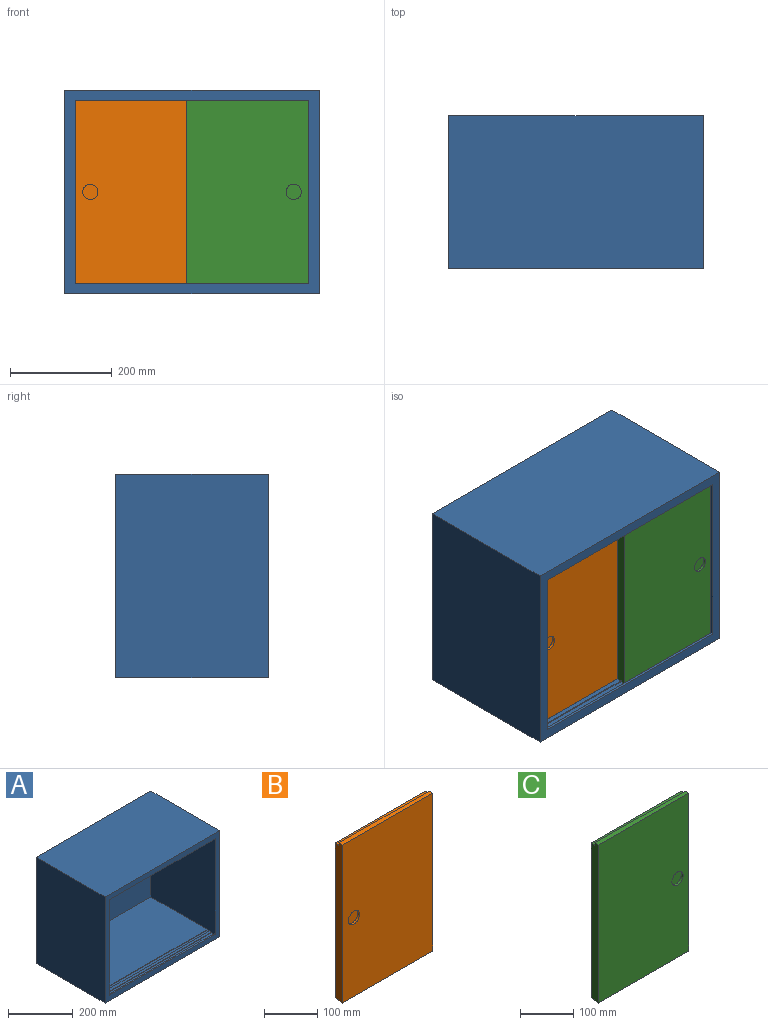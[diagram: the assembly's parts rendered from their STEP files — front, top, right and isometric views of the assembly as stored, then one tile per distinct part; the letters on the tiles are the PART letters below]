
ASSEMBLY  parts=3 mates=2
PART A: 27 faces, bbox 500x300x400 mm
  f0: plane 460x10mm, normal (0,0,-1), area 4600mm2, adj f10,f12,f21,f24
  f1: plane 460x245mm, normal (0,0,-1), area 112700mm2, adj f10,f11,f12,f22
  f2: plane 460x10mm, normal (0,0,1), area 4600mm2, adj f10,f12,f17,f19
  f3: plane 460x245mm, normal (0,0,1), area 112700mm2, adj f10,f11,f12,f16
  f4: plane 500x400mm, normal (0,-1,0), area 34400mm2, adj f5,f7,f8,f9,f10,f12,f13,f14
  f5: plane 400x300mm, normal (1,0,0), area 120000mm2, adj f4,f6,f8,f9
  f6: plane 500x400mm, normal (0,1,0), area 200000mm2, adj f5,f7,f8,f9
  f7: plane 400x300mm, normal (-1,0,0), area 120000mm2, adj f4,f6,f8,f9
  f8: plane 500x300mm, normal (0,0,1), area 150000mm2, adj f4,f5,f6,f7
  f9: plane 500x300mm, normal (0,0,-1), area 150000mm2, adj f4,f5,f6,f7
  f10: plane 367x280mm, normal (-1,0,0), area 100940mm2, adj f0,f1,f2,f3,f4,f11,f13,f14
  f11: plane 460x360mm, normal (0,-1,0), area 165600mm2, adj f1,f3,f10,f12
  f12: plane 367x280mm, normal (1,0,0), area 100940mm2, adj f0,f1,f2,f3,f4,f11,f13,f14
  f13: plane 460x5mm, normal (0,0,-1), area 2300mm2, adj f4,f10,f12,f25
  f14: plane 460x5mm, normal (0,0,1), area 2300mm2, adj f4,f10,f12,f20
  f15: plane 460x10mm, normal (0,0,1), area 4600mm2, adj f10,f12,f16,f17
  f16: plane 460x2mm, normal (0,-1,0), area 920mm2, adj f3,f10,f12,f15
  f17: plane 460x2mm, normal (0,1,0), area 920mm2, adj f2,f10,f12,f15
  f18: plane 460x10mm, normal (0,0,1), area 4600mm2, adj f10,f12,f19,f20
  f19: plane 460x2mm, normal (0,-1,0), area 920mm2, adj f2,f10,f12,f18
  f20: plane 460x2mm, normal (0,1,0), area 920mm2, adj f10,f12,f14,f18
  f21: plane 460x5mm, normal (0,1,0), area 2300mm2, adj f0,f10,f12,f23
  f22: plane 460x5mm, normal (0,-1,0), area 2300mm2, adj f1,f10,f12,f23
  f23: plane 460x10mm, normal (0,0,-1), area 4600mm2, adj f10,f12,f21,f22
  f24: plane 460x5mm, normal (0,-1,0), area 2300mm2, adj f0,f10,f12,f26
  f25: plane 460x5mm, normal (0,1,0), area 2300mm2, adj f10,f12,f13,f26
  f26: plane 460x10mm, normal (0,0,-1), area 4600mm2, adj f10,f12,f24,f25
PART B: 12 faces, bbox 240x20x364.5 mm
  f0: plane 240x5mm, normal (0,1,0), area 1200mm2, adj f2,f3,f8,f9
  f1: plane 364.5x240mm, normal (0,-1,0), area 86773.1mm2, adj f2,f3,f5,f8,f10
  f2: plane 364.5x20mm, normal (1,0,0), area 7220mm2, adj f0,f1,f4,f5,f6,f7,f8,f9
  f3: plane 364.5x20mm, normal (-1,0,0), area 7220mm2, adj f0,f1,f4,f5,f6,f7,f8,f9
  f4: plane 357.5x240mm, normal (0,1,0), area 85800mm2, adj f2,f3,f7,f9
  f5: plane 240x10mm, normal (0,0,-1), area 2400mm2, adj f1,f2,f3,f6
  f6: plane 240x2mm, normal (0,1,0), area 480mm2, adj f2,f3,f5,f7
  f7: plane 240x10mm, normal (0,0,-1), area 2400mm2, adj f2,f3,f4,f6
  f8: plane 240x10mm, normal (0,0,1), area 2400mm2, adj f0,f1,f2,f3
  f9: plane 240x10mm, normal (0,0,1), area 2400mm2, adj f0,f2,f3,f4
  f10: cylinder r=15mm len=30mm, axis (0,-1,0), area 471.2mm2, adj f1,f11
  f11: plane 30x30mm, normal (0,-1,0), area 706.9mm2, adj f10
PART C: 12 faces, bbox 240x20x364.5 mm
  f0: plane 364.5x240mm, normal (0,-1,0), area 86773.1mm2, adj f3,f4,f7,f8,f10
  f1: plane 357.5x240mm, normal (0,1,0), area 85800mm2, adj f3,f6,f7,f9
  f2: plane 240x5mm, normal (0,1,0), area 1200mm2, adj f3,f7,f8,f9
  f3: plane 364.5x20mm, normal (-1,0,0), area 7220mm2, adj f0,f1,f2,f4,f5,f6,f8,f9
  f4: plane 240x10mm, normal (0,0,-1), area 2400mm2, adj f0,f3,f5,f7
  f5: plane 240x2mm, normal (0,1,0), area 480mm2, adj f3,f4,f6,f7
  f6: plane 240x10mm, normal (0,0,-1), area 2400mm2, adj f1,f3,f5,f7
  f7: plane 364.5x20mm, normal (1,0,0), area 7220mm2, adj f0,f1,f2,f4,f5,f6,f8,f9
  f8: plane 240x10mm, normal (0,0,1), area 2400mm2, adj f0,f2,f3,f7
  f9: plane 240x10mm, normal (0,0,1), area 2400mm2, adj f1,f2,f3,f7
  f10: cylinder r=15mm len=30mm, axis (0,-1,0), area 471.2mm2, adj f0,f11
  f11: plane 30x30mm, normal (0,-1,0), area 706.9mm2, adj f10
PLACE A at identity fixed
PLACE B at identity
PLACE C at identity
MATE slider A.f10 <-> C.f7  axis (-1,0,0) through (230,-135,20)mm
MATE slider A.f12 <-> B.f3  axis (1,0,0) through (-230,-115,20)mm
